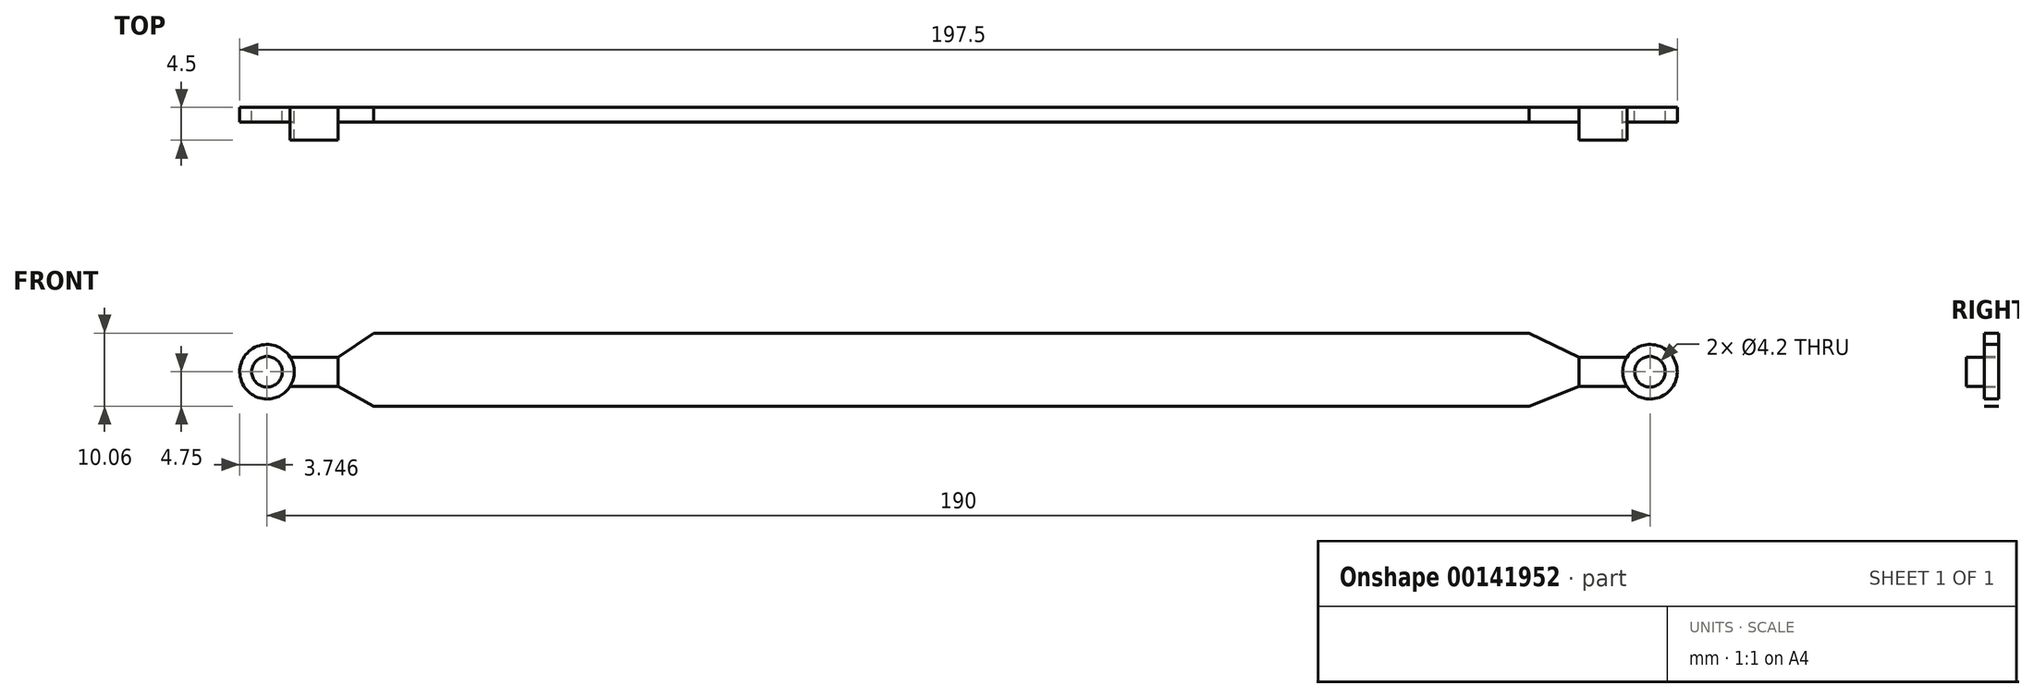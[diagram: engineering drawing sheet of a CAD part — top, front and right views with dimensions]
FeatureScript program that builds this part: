
annotation { "Feature Type Name" : "Feature", "Feature Type Description" : "" }
export const myFeature = defineFeature(function(context is Context, id is Id, definition is map)
    precondition{}
    {
        {
            var Q0;
            Q0=qCreatedBy(makeId("Front.planeOp"),FACE);
            var sketch = newSketch(context, id + "F0", { "sketchPlane" : qUnion([Q0])});
            skCircle(sketch, "E0", {"center": v(-40.78, 0) * mm, "radius": 2.1 * mm});
            skCircle(sketch, "E1", {"center": v(-40.78, 0) * mm, "radius": 3.75 * mm});
            skLineSegment(sketch, "E2", {"start": v(-37.61, 2) * mm, "end": v(-31.03, 2) * mm});
            skLineSegment(sketch, "E3", {"start": v(-31.03, 2) * mm, "end": v(-31.03, -2) * mm});
            skLineSegment(sketch, "E4", {"start": v(-31.03, -2) * mm, "end": v(-37.61, -2) * mm});
            skCircle(sketch, "E5", {"center": v(149.22, 0) * mm, "radius": 2.1 * mm});
            skCircle(sketch, "E6", {"center": v(149.22, 0) * mm, "radius": 3.75 * mm});
            skLineSegment(sketch, "E7", {"start": v(146.04, 2) * mm, "end": v(139.47, 2) * mm});
            skLineSegment(sketch, "E8", {"start": v(139.47, 2) * mm, "end": v(139.47, -2) * mm});
            skLineSegment(sketch, "E9", {"start": v(139.47, -2) * mm, "end": v(146.04, -2) * mm});
            skLineSegment(sketch, "E10", {"start": v(-31.03, -2) * mm, "end": v(-26.15, -4.75) * mm});
            skLineSegment(sketch, "E11", {"start": v(-26.15, -4.75) * mm, "end": v(132.63, -4.75) * mm});
            skLineSegment(sketch, "E12", {"start": v(132.63, -4.75) * mm, "end": v(139.47, -2) * mm});
            skLineSegment(sketch, "E13", {"start": v(139.47, 2) * mm, "end": v(132.63, 5.31) * mm});
            skLineSegment(sketch, "E14", {"start": v(132.63, 5.31) * mm, "end": v(-26.15, 5.31) * mm});
            skLineSegment(sketch, "E15", {"start": v(-26.15, 5.31) * mm, "end": v(-31.03, 2) * mm});
            skSolve(sketch);
        }
        {
            var Q0;
            Q0=makeQuery(id+"F0.imprint","IMPRINT",FACE,{"disambiguationData":[TD([[makeQuery(id+"F0.imprint","IMPRINT",EDGE,{"derivedFrom":sQuery(id+"F0.wireOp",EDGE,"E0")}),-1.0]])]});
            var Q1;
            Q1=makeQuery(id+"F0.imprint","IMPRINT",FACE,{"disambiguationData":[TD([[makeQuery(id+"F0.imprint","IMPRINT",EDGE,{"derivedFrom":sQuery(id+"F0.wireOp",EDGE,"E5")}),-1.0]])]});
            extrude(context, id + "F1", {"entities" : qUnion([Q0, Q1]), "depth" : 2 * mm, "offsetDistance" : 25 * mm});
        }
        {
            var Q0;
            {var subQ0=sQuery(id+"F0.wireOp",EDGE,"E7");Q0=makeQuery(id+"F0.imprint","IMPRINT",FACE,{"disambiguationData":[TD([[makeQuery(id+"F0.imprint","IMPRINT",EDGE,{"derivedFrom":subQ0}),1.0]])]});}
            var Q1;
            {var subQ0=sQuery(id+"F0.wireOp",EDGE,"E2");Q1=makeQuery(id+"F0.imprint","IMPRINT",FACE,{"disambiguationData":[TD([[makeQuery(id+"F0.imprint","IMPRINT",EDGE,{"derivedFrom":subQ0}),-1.0]])]});}
            extrude(context, id + "F2", {"entities" : qUnion([Q0, Q1]), "depth" : 4.5 * mm, "offsetDistance" : 25 * mm});
        }
        {
            var Q0;
            Q0=makeQuery(id+"F0.imprint","IMPRINT",FACE,{"disambiguationData":[TD([[makeQuery(id+"F0.imprint","IMPRINT",EDGE,{"derivedFrom":sQuery(id+"F0.wireOp",EDGE,"E3")}),1.0]])]});
            extrude(context, id + "F3", {"entities" : qUnion([Q0]), "depth" : 2 * mm, "offsetDistance" : 25 * mm});
        }
    });
